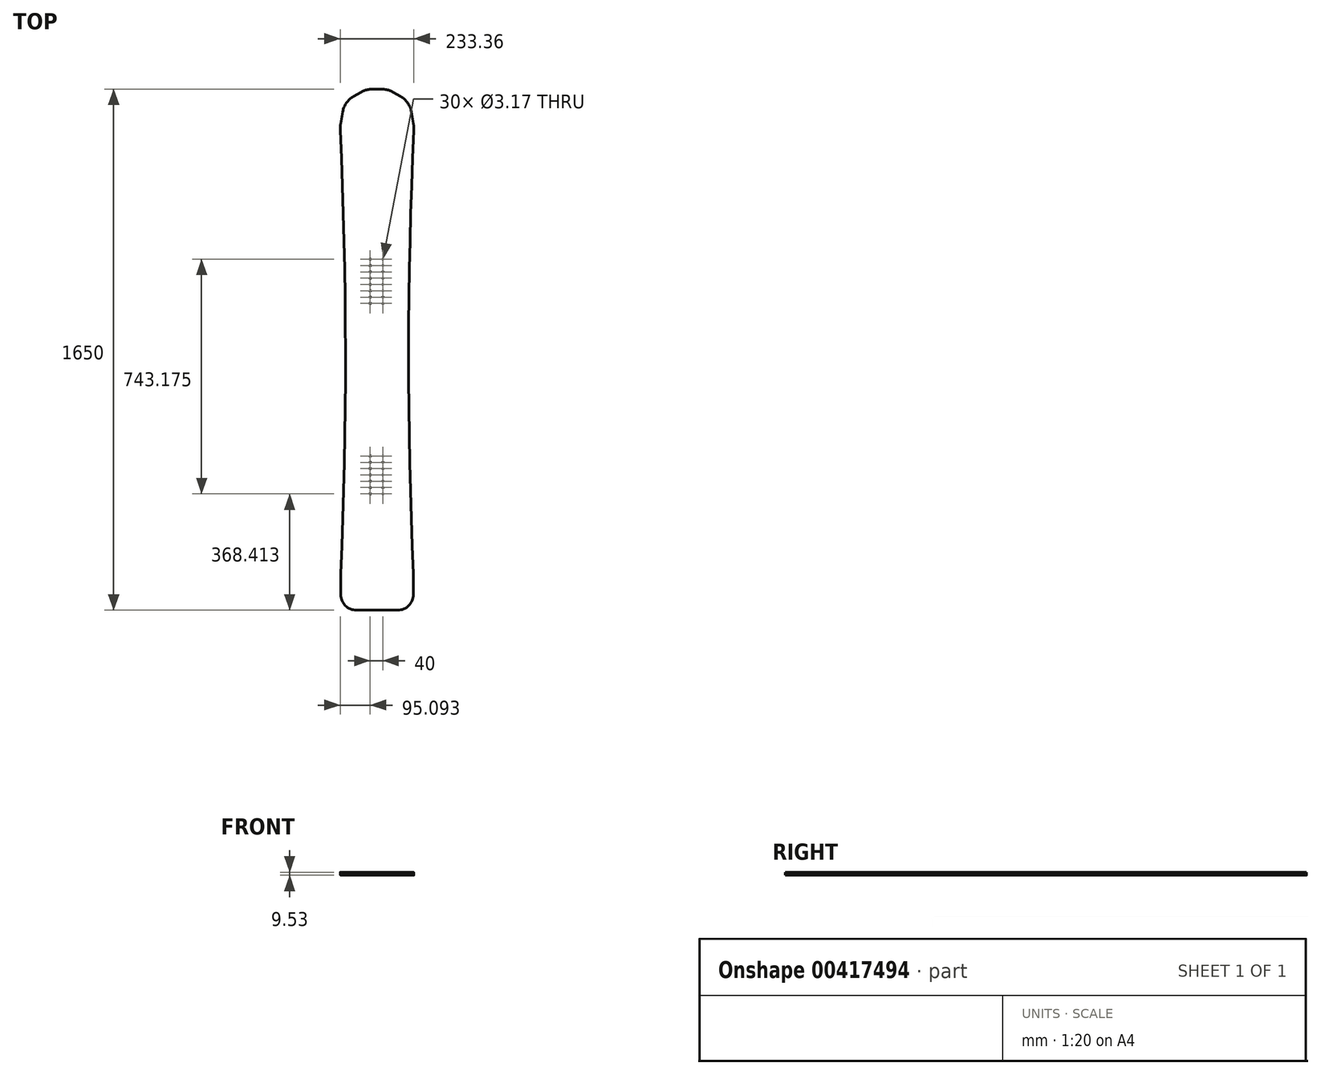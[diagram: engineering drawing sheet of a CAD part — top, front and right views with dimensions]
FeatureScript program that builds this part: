
annotation { "Feature Type Name" : "Feature", "Feature Type Description" : "" }
export const myFeature = defineFeature(function(context is Context, id is Id, definition is map)
    precondition{}
    {
        {
            var Q0;
            Q0=qCreatedBy(makeId("Top.planeOp"),FACE);
            var sketch = newSketch(context, id + "F0", { "sketchPlane" : qUnion([Q0])});
            skLineSegment(sketch, "E0", {"start": v(0, 0) * mm, "end": v(0, 1524) * mm, "construction": true});
            skLineSegment(sketch, "E1", {"start": v(0, 0) * mm, "end": v(5080, 0) * mm, "construction": true});
            skLineSegment(sketch, "E2", {"start": v(100, 0) * mm, "end": v(100, 1270) * mm, "construction": true});
            skLineSegment(sketch, "E3.MirrorCS", {"start": v(100, 0) * mm, "end": v(100, -1270) * mm, "construction": true});
            skLineSegment(sketch, "E4.MirrorCS", {"start": v(-100, 0) * mm, "end": v(-100, 1270) * mm, "construction": true});
            skLineSegment(sketch, "E5.MirrorCS", {"start": v(-100, 0) * mm, "end": v(-100, -1270) * mm, "construction": true});
            skLineSegment(sketch, "E6.MirrorCS", {"start": v(0, 0) * mm, "end": v(-5080, 0) * mm, "construction": true});
            skLineSegment(sketch, "E7.MirrorCS", {"start": v(0, 0) * mm, "end": v(0, -1524) * mm, "construction": true});
            skLineSegment(sketch, "E8", {"start": v(-1415.62, 850) * mm, "end": v(1956.8, 850) * mm, "construction": true});
            skLineSegment(sketch, "E9", {"start": v(-1574.94, -850) * mm, "end": v(1802.27, -850) * mm, "construction": true});
            skLineSegment(sketch, "E10", {"start": v(-861.83, 730) * mm, "end": v(882.87, 730) * mm, "construction": true});
            skLineSegment(sketch, "E11", {"start": v(-637.12, -800) * mm, "end": v(539.37, -800) * mm, "construction": true});
            skPoint(sketch, "E12.startSnap0", {"position": v(113.67, -850) * mm});
            skSolve(sketch);
        }
        {
            var Q0;
            Q0=qCreatedBy(makeId("Top.planeOp"),FACE);
            var sketch = newSketch(context, id + "F1", { "sketchPlane" : qUnion([Q0])});
            skPoint(sketch, "E13", {"position": v(-15700, 0) * mm});
            skPoint(sketch, "E14.MirrorP", {"position": v(15700, 0) * mm});
            skPoint(sketch, "E15", {"position": v(-100, 0) * mm});
            skArc(sketch, "E16", {"start": v(-115, -683.94) * mm, "mid": v(-100, 17.52) * mm, "end": v(-116.58, 718.95) * mm});
            skArc(sketch, "E17.MirrorC", {"start": v(115, -683.94) * mm, "mid": v(100, 17.52) * mm, "end": v(116.58, 718.95) * mm});
            skLineSegment(sketch, "E18", {"start": v(0, 850) * mm, "end": v(-16.24, 850) * mm});
            skLineSegment(sketch, "E19", {"start": v(-51.24, 840.62) * mm, "end": v(-74.57, 827.16) * mm});
            skPoint(sketch, "E20", {"position": v(-117.09, 730) * mm});
            skLineSegment(sketch, "E21", {"start": v(-115.16, 740.93) * mm, "end": v(-108.5, 778.69) * mm});
            skPoint(sketch, "E22.visualSharp", {"position": v(-35, 850) * mm});
            skArc(sketch, "E22.filletArc", {"start": v(-16.24, 850) * mm, "mid": v(-34.36, 847.61) * mm, "end": v(-51.24, 840.62) * mm});
            skPoint(sketch, "E23.visualSharp", {"position": v(-102.84, 810.83) * mm});
            skArc(sketch, "E23.filletArc", {"start": v(-74.57, 827.16) * mm, "mid": v(-96.9, 806.68) * mm, "end": v(-108.5, 778.69) * mm});
            skLineSegment(sketch, "E24.MirrorCS", {"start": v(0, 850) * mm, "end": v(16.24, 850) * mm});
            skPoint(sketch, "E25.MirrorP", {"position": v(35, 850) * mm});
            skLineSegment(sketch, "E26.MirrorCS", {"start": v(51.24, 840.62) * mm, "end": v(74.57, 827.16) * mm});
            skArc(sketch, "E27.MirrorCS", {"start": v(74.57, 827.16) * mm, "mid": v(96.9, 806.68) * mm, "end": v(108.5, 778.69) * mm});
            skArc(sketch, "E28.MirrorCS", {"start": v(16.24, 850) * mm, "mid": v(34.36, 847.61) * mm, "end": v(51.24, 840.62) * mm});
            skLineSegment(sketch, "E29.MirrorCS", {"start": v(115.16, 740.93) * mm, "end": v(108.5, 778.69) * mm});
            skLineSegment(sketch, "E30", {"start": v(0, -800) * mm, "end": v(-65, -800) * mm});
            skLineSegment(sketch, "E31.MirrorCS", {"start": v(0, -800) * mm, "end": v(65, -800) * mm});
            skLineSegment(sketch, "E32", {"start": v(-115, -750) * mm, "end": v(-115, -683.94) * mm});
            skLineSegment(sketch, "E33.MirrorCS", {"start": v(115, -750) * mm, "end": v(115, -683.94) * mm});
            skPoint(sketch, "E34.visualSharp", {"position": v(-115, -800) * mm});
            skArc(sketch, "E34.filletArc", {"start": v(-115, -750) * mm, "mid": v(-100.36, -785.36) * mm, "end": v(-65, -800) * mm});
            skPoint(sketch, "E35.visualSharp", {"position": v(115, -800) * mm});
            skArc(sketch, "E35.filletArc", {"start": v(65, -800) * mm, "mid": v(100.36, -785.36) * mm, "end": v(115, -750) * mm});
            skArc(sketch, "E36.filletArc", {"start": v(-115.16, 740.93) * mm, "mid": v(-116.48, 729.98) * mm, "end": v(-116.58, 718.95) * mm});
            skPoint(sketch, "E37.visualSharp", {"position": v(117.09, 730) * mm});
            skArc(sketch, "E37.filletArc", {"start": v(116.58, 718.95) * mm, "mid": v(116.48, 729.98) * mm, "end": v(115.16, 740.93) * mm});
            skSolve(sketch);
        }
        {
            var Q0;
            Q0=makeQuery(id+"F1.imprint","IMPRINT",FACE,{"disambiguationData":[TD([[makeQuery(id+"F1.imprint","IMPRINT",EDGE,{"derivedFrom":sQuery(id+"F1.wireOp",EDGE,"E16")}),-1.0]])]});
            extrude(context, id + "F2", {"entities" : qUnion([Q0]), "depth" : 9.52 * mm});
        }
        {
            var Q0;
            Q0=makeQuery(id+"F2.opExtrude","CAP_FACE",FACE,{"disambiguationData":[OSD([sQuery(id+"F1.wireOp",EDGE,"E16"),sQuery(id+"F1.wireOp",EDGE,"E17.MirrorC"),sQuery(id+"F1.wireOp",EDGE,"E18"),sQuery(id+"F1.wireOp",EDGE,"E19"),sQuery(id+"F1.wireOp",EDGE,"E21"),sQuery(id+"F1.wireOp",EDGE,"E22.filletArc"),sQuery(id+"F1.wireOp",EDGE,"E23.filletArc"),sQuery(id+"F1.wireOp",EDGE,"E24.MirrorCS"),sQuery(id+"F1.wireOp",EDGE,"E26.MirrorCS"),sQuery(id+"F1.wireOp",EDGE,"E27.MirrorCS"),sQuery(id+"F1.wireOp",EDGE,"E28.MirrorCS"),sQuery(id+"F1.wireOp",EDGE,"E29.MirrorCS"),sQuery(id+"F1.wireOp",EDGE,"E30"),sQuery(id+"F1.wireOp",EDGE,"E31.MirrorCS"),sQuery(id+"F1.wireOp",EDGE,"E32"),sQuery(id+"F1.wireOp",EDGE,"E33.MirrorCS"),sQuery(id+"F1.wireOp",EDGE,"E34.filletArc"),sQuery(id+"F1.wireOp",EDGE,"E35.filletArc"),sQuery(id+"F1.wireOp",EDGE,"E36.filletArc"),sQuery(id+"F1.wireOp",EDGE,"E37.filletArc")])],"isStart":false});
            var sketch = newSketch(context, id + "F3", { "sketchPlane" : qUnion([Q0])});
            skLineSegment(sketch, "E38", {"start": v(-125, 0) * mm, "end": v(125, 0) * mm, "construction": true});
            skLineSegment(sketch, "E39", {"start": v(0, 0) * mm, "end": v(0, 455.87) * mm, "construction": true});
            skLineSegment(sketch, "E40", {"start": v(-125, -60) * mm, "end": v(125, -60) * mm, "construction": true});
            skCircle(sketch, "E41", {"center": v(-21.59, 171.59) * mm, "radius": 1.59 * mm});
            skCircle(sketch, "E42.0.1.0", {"center": v(-21.59, 191.59) * mm, "radius": 1.59 * mm});
            skCircle(sketch, "E42.0.2.0", {"center": v(-21.59, 211.59) * mm, "radius": 1.59 * mm});
            skCircle(sketch, "E42.0.3.0", {"center": v(-21.59, 231.59) * mm, "radius": 1.59 * mm});
            skCircle(sketch, "E42.0.4.0", {"center": v(-21.59, 251.59) * mm, "radius": 1.59 * mm});
            skCircle(sketch, "E42.0.5.0", {"center": v(-21.59, 271.59) * mm, "radius": 1.59 * mm});
            skCircle(sketch, "E42.0.6.0", {"center": v(-21.59, 291.59) * mm, "radius": 1.59 * mm});
            skCircle(sketch, "E42.0.7.0", {"center": v(-21.59, 311.59) * mm, "radius": 1.59 * mm});
            skCircle(sketch, "E42.1.0.0", {"center": v(18.41, 171.59) * mm, "radius": 1.59 * mm});
            skCircle(sketch, "E42.1.1.0", {"center": v(18.41, 191.59) * mm, "radius": 1.59 * mm});
            skCircle(sketch, "E42.1.2.0", {"center": v(18.41, 211.59) * mm, "radius": 1.59 * mm});
            skCircle(sketch, "E42.1.3.0", {"center": v(18.41, 231.59) * mm, "radius": 1.59 * mm});
            skCircle(sketch, "E42.1.4.0", {"center": v(18.41, 251.59) * mm, "radius": 1.59 * mm});
            skCircle(sketch, "E42.1.5.0", {"center": v(18.41, 271.59) * mm, "radius": 1.59 * mm});
            skCircle(sketch, "E42.1.6.0", {"center": v(18.41, 291.59) * mm, "radius": 1.59 * mm});
            skCircle(sketch, "E42.1.7.0", {"center": v(18.41, 311.59) * mm, "radius": 1.59 * mm});
            skLineSegment(sketch, "E42.direction1", {"start": v(-21.59, 171.59) * mm, "end": v(18.41, 171.59) * mm, "construction": true});
            skLineSegment(sketch, "E42.direction2", {"start": v(-21.59, 171.59) * mm, "end": v(-21.59, 191.59) * mm, "construction": true});
            skCircle(sketch, "E43.MirrorC", {"center": v(-21.59, -311.59) * mm, "radius": 1.59 * mm});
            skCircle(sketch, "E44.MirrorC", {"center": v(18.41, -431.59) * mm, "radius": 1.59 * mm});
            skCircle(sketch, "E45.MirrorC", {"center": v(18.41, -371.59) * mm, "radius": 1.59 * mm});
            skCircle(sketch, "E46.MirrorC", {"center": v(-21.59, -331.59) * mm, "radius": 1.59 * mm});
            skCircle(sketch, "E47.MirrorC", {"center": v(-21.59, -371.59) * mm, "radius": 1.59 * mm});
            skCircle(sketch, "E48.MirrorC", {"center": v(-21.59, -431.59) * mm, "radius": 1.59 * mm});
            skCircle(sketch, "E49.MirrorC", {"center": v(18.41, -331.59) * mm, "radius": 1.59 * mm});
            skCircle(sketch, "E50.MirrorC", {"center": v(-21.59, -351.59) * mm, "radius": 1.59 * mm});
            skCircle(sketch, "E51.MirrorC", {"center": v(18.41, -411.59) * mm, "radius": 1.59 * mm});
            skCircle(sketch, "E52.MirrorC", {"center": v(-21.59, -411.59) * mm, "radius": 1.59 * mm});
            skCircle(sketch, "E53.MirrorC", {"center": v(-21.59, -391.59) * mm, "radius": 1.59 * mm});
            skCircle(sketch, "E54.MirrorC", {"center": v(18.41, -391.59) * mm, "radius": 1.59 * mm});
            skCircle(sketch, "E55.MirrorC", {"center": v(18.41, -351.59) * mm, "radius": 1.59 * mm});
            skCircle(sketch, "E56.MirrorC", {"center": v(18.41, -311.59) * mm, "radius": 1.59 * mm});
            skLineSegment(sketch, "E57.MirrorCS", {"start": v(-21.59, -291.59) * mm, "end": v(-21.59, -311.59) * mm, "construction": true});
            skLineSegment(sketch, "E58.MirrorCS", {"start": v(-21.59, -291.59) * mm, "end": v(18.41, -291.59) * mm, "construction": true});
            skSolve(sketch);
        }
        {
            var Q0;
            Q0 = qSketchRegion(id + "F3", true);
            extrude(context, id + "F4", {"entities" : qUnion([Q0]), "operationType" : NewBodyOperationType.REMOVE, "endBound" : BoundingType.UP_TO_NEXT, "oppositeDirection" : true, "depth" : 25 * mm});
        }
    });
